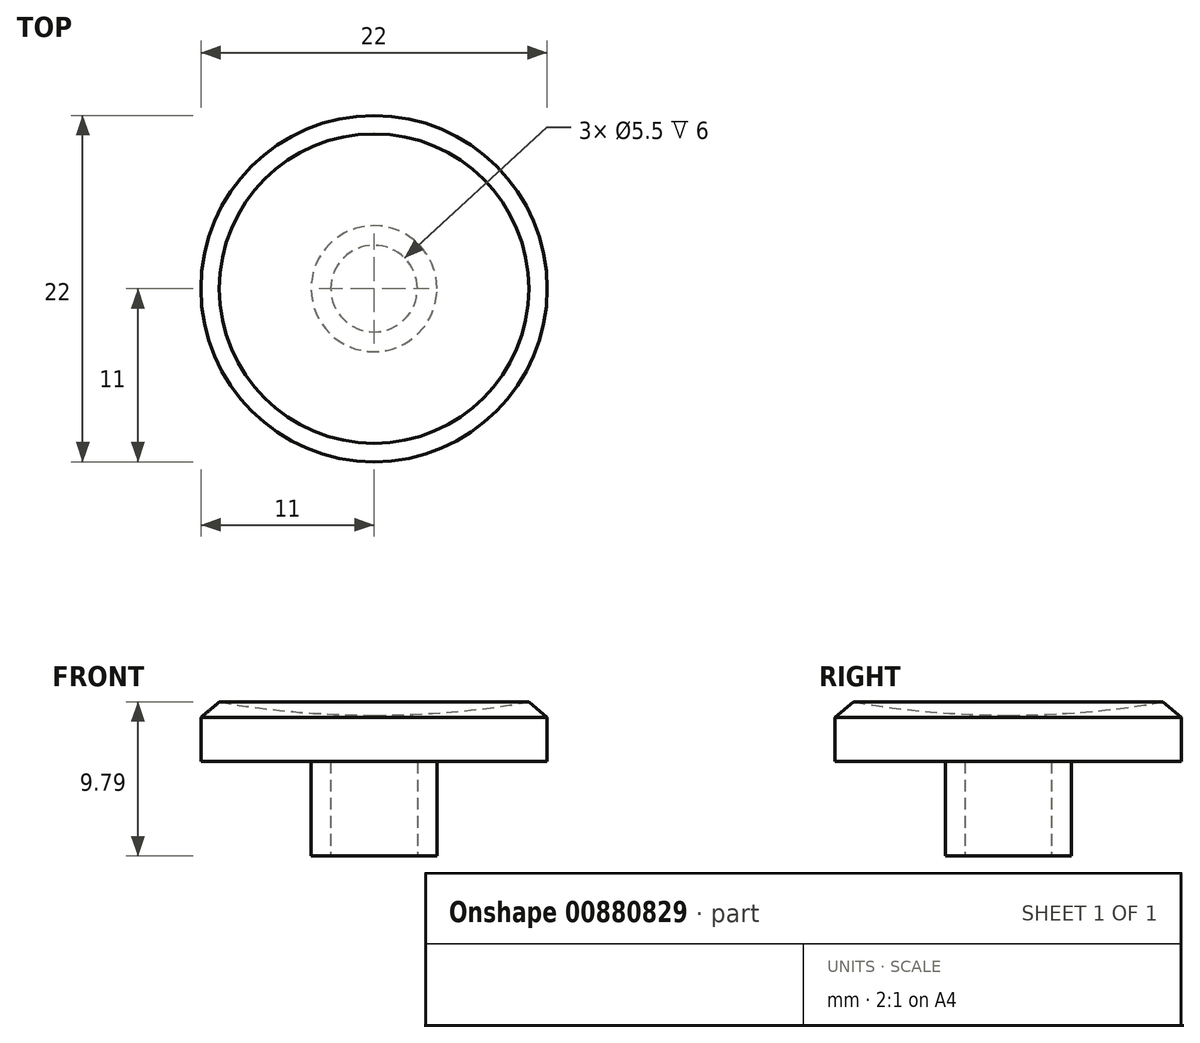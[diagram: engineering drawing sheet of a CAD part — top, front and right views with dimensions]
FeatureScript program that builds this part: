
annotation { "Feature Type Name" : "Feature", "Feature Type Description" : "" }
export const myFeature = defineFeature(function(context is Context, id is Id, definition is map)
    precondition{}
    {
        {
            var Q0;
            Q0=qCreatedBy(makeId("Front.planeOp"),FACE);
            var sketch = newSketch(context, id + "F0", { "sketchPlane" : qUnion([Q0])});
            skLineSegment(sketch, "E0.0", {"start": v(-4, 0) * mm, "end": v(-4, 6) * mm});
            skLineSegment(sketch, "E1", {"start": v(-4, 6) * mm, "end": v(-11, 6) * mm});
            skLineSegment(sketch, "E2", {"start": v(0, 0) * mm, "end": v(0, 8.94) * mm});
            skLineSegment(sketch, "E3.0", {"start": v(-11, 6) * mm, "end": v(-11, 10) * mm});
            skLineSegment(sketch, "E4", {"start": v(-4, 0) * mm, "end": v(0, 0) * mm});
            skArc(sketch, "E5", {"start": v(-11, 10) * mm, "mid": v(-5.53, 9.2) * mm, "end": v(0, 8.94) * mm});
            skSolve(sketch);
        }
        {
            var Q0;
            Q0 = qSketchRegion(id + "F0", true);
            var Q1;
            Q1=sQuery(id+"F0.wireOp",EDGE,"E2");
            revolve(context, id + "F1", {"surfaceOperationType" : NewSurfaceOperationType.NEW, "entities" : qUnion([Q0]), "axis" : qUnion([Q1]), "revolveType" : RevolveType.FULL});
        }
        {
            var Q0;
            Q0=makeQuery(id+"F1.opRevolve","SWEPT_EDGE",EDGE,{"disambiguationData":[OSD([sQuery(id+"F0.wireOp",EDGE,"E3.0"),sQuery(id+"F0.wireOp",EDGE,"E5")])]});
            chamfer(context, id + "F2", {"entities" : qUnion([Q0]), "width" : 1 * mm, "tangentPropagation" : true});
        }
        {
            var Q0;
            Q0=makeQuery(id+"F1.opRevolve","SWEPT_FACE",FACE,{"disambiguationData":[OSD([sQuery(id+"F0.wireOp",EDGE,"E4")])]});
            var sketch = newSketch(context, id + "F3", { "sketchPlane" : qUnion([Q0])});
            skCircle(sketch, "E6", {"center": v(0, 0) * mm, "radius": 2.75 * mm});
            skSolve(sketch);
        }
        {
            var Q0;
            Q0 = qSketchRegion(id + "F3", true);
            extrude(context, id + "F4", {"entities" : qUnion([Q0]), "operationType" : NewBodyOperationType.REMOVE, "oppositeDirection" : true, "depth" : 6 * mm, "offsetDistance" : 25 * mm});
        }
    });
